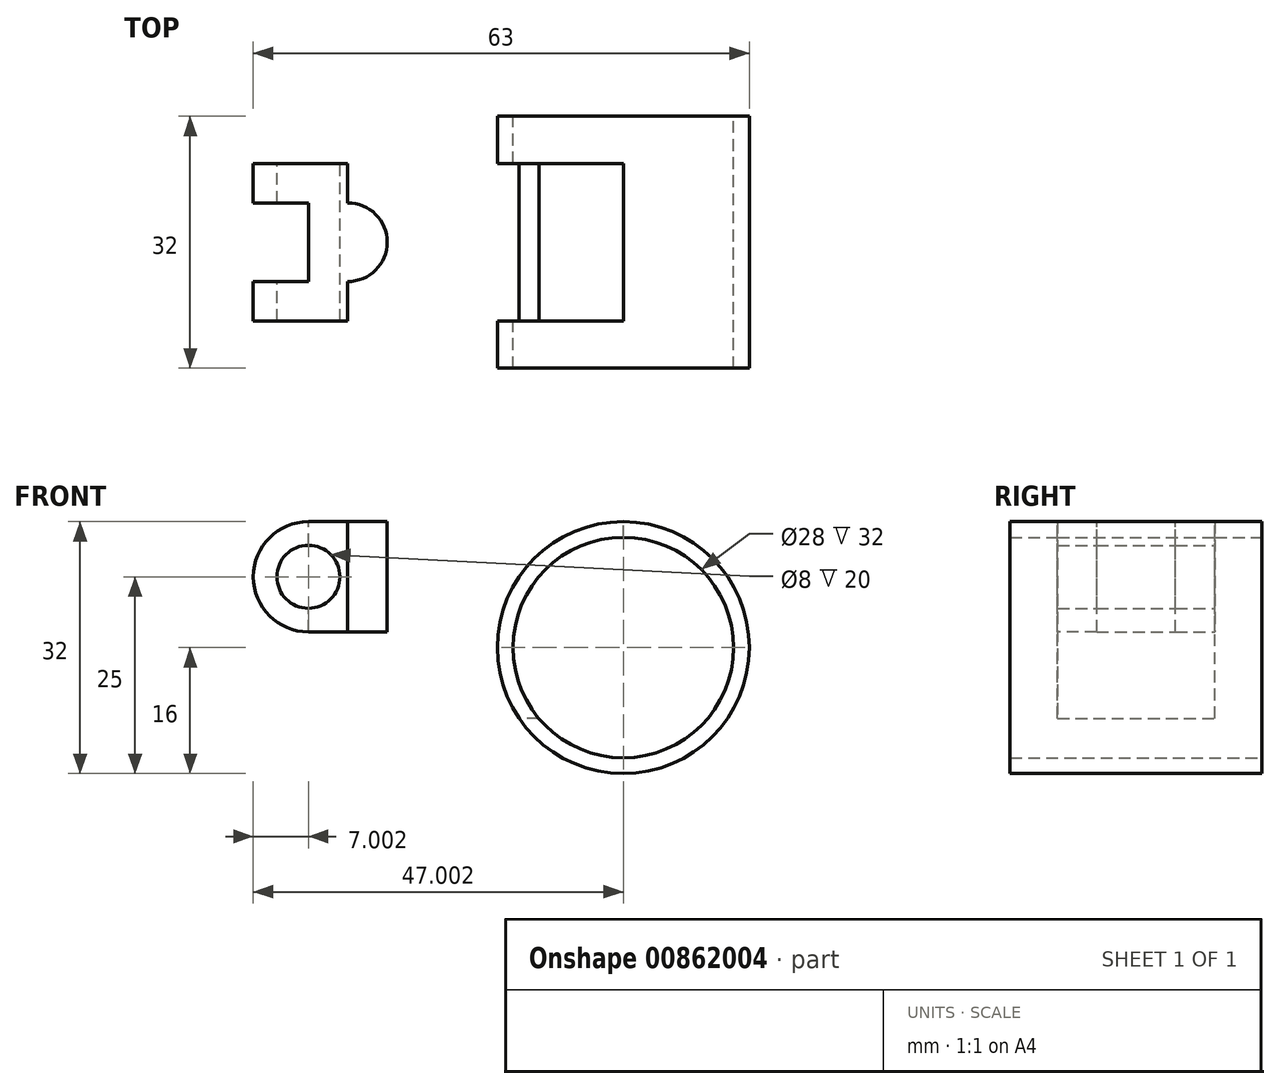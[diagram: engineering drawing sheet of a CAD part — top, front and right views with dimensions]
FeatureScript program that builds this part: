
annotation { "Feature Type Name" : "Feature", "Feature Type Description" : "" }
export const myFeature = defineFeature(function(context is Context, id is Id, definition is map)
    precondition{}
    {
        {
            var Q0;
            Q0=qCreatedBy(makeId("Front.planeOp"),FACE);
            var sketch = newSketch(context, id + "F0", { "sketchPlane" : qUnion([Q0])});
            skCircle(sketch, "E0", {"center": v(23.31, 0) * mm, "radius": 16 * mm});
            skCircle(sketch, "E1", {"center": v(23.31, 0) * mm, "radius": 14 * mm});
            skLineSegment(sketch, "E2", {"start": v(23.31, 16) * mm, "end": v(-16.69, 16) * mm});
            skLineSegment(sketch, "E3", {"start": v(-16.69, 2) * mm, "end": v(7.44, 2) * mm});
            skArc(sketch, "E4", {"start": v(-16.69, 16) * mm, "mid": v(-23.69, 9) * mm, "end": v(-16.69, 2) * mm});
            skCircle(sketch, "E5", {"center": v(-16.69, 9) * mm, "radius": 4 * mm});
            skSolve(sketch);
        }
        {
            var Q0;
            Q0=makeQuery(id+"F0.imprint","IMPRINT",FACE,{"disambiguationData":[TD([[makeQuery(id+"F0.imprint","IMPRINT",EDGE,{"derivedFrom":sQuery(id+"F0.wireOp",EDGE,"E1")}),-1.0]])]});
            extrude(context, id + "F1", {"entities" : qUnion([Q0]), "endBound" : BoundingType.SYMMETRIC, "depth" : 32 * mm, "offsetDistance" : 25 * mm});
        }
        {
            var Q0;
            {var subQ1=sQuery(id+"F0.wireOp",EDGE,"E2");Q0=makeQuery(id+"F0.imprint","IMPRINT",FACE,{"disambiguationData":[TD([[makeQuery(id+"F0.imprint","IMPRINT",EDGE,{"derivedFrom":subQ1}),1.0]])]});}
            extrude(context, id + "F2", {"entities" : qUnion([Q0]), "operationType" : NewBodyOperationType.ADD, "endBound" : BoundingType.SYMMETRIC, "depth" : 20 * mm, "offsetDistance" : 25 * mm});
        }
        {
            var Q0;
            Q0=makeQuery(id+"F2.opExtrude","SWEPT_FACE",FACE,{"disambiguationData":[OSD([sQuery(id+"F0.wireOp",EDGE,"E2")])]});
            var sketch = newSketch(context, id + "F3", { "sketchPlane" : qUnion([Q0])});
            skLineSegment(sketch, "E6", {"start": v(-16.69, 10) * mm, "end": v(-11.69, 10) * mm});
            skLineSegment(sketch, "E7", {"start": v(-11.69, 10) * mm, "end": v(-11.69, 5) * mm});
            skLineSegment(sketch, "E8", {"start": v(-11.69, -5) * mm, "end": v(-11.69, -10) * mm});
            skArc(sketch, "E9", {"start": v(-11.69, 5) * mm, "mid": v(-6.69, 0) * mm, "end": v(-11.69, -5) * mm});
            skLineSegment(sketch, "E10", {"start": v(-11.69, 5) * mm, "end": v(-26.69, 5) * mm});
            skLineSegment(sketch, "E11", {"start": v(-11.69, -5) * mm, "end": v(-26.69, -5) * mm});
            skLineSegment(sketch, "E12", {"start": v(-26.69, -5) * mm, "end": v(-26.69, 5) * mm});
            skSolve(sketch);
        }
        {
            var Q0;
            {var subQ0=sQuery(id+"F3.wireOp",EDGE,"E12");Q0=makeQuery(id+"F3.imprint","IMPRINT",FACE,{"disambiguationData":[TD([[makeQuery(id+"F3.imprint","IMPRINT",EDGE,{"derivedFrom":subQ0}),-1.0]])]});}
            var Q1;
            {var subQ0=sQuery(id+"F3.wireOp",EDGE,"E9");Q1=makeQuery(id+"F3.imprint","IMPRINT",FACE,{"disambiguationData":[TD([[makeQuery(id+"F3.imprint","IMPRINT",EDGE,{"derivedFrom":subQ0}),-1.0]])]});}
            extrude(context, id + "F4", {"entities" : qUnion([Q0, Q1]), "operationType" : NewBodyOperationType.REMOVE, "oppositeDirection" : true, "depth" : 25 * mm, "offsetDistance" : 25 * mm});
        }
    });
